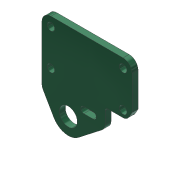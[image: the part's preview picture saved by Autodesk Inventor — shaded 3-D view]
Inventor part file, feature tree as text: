
AUTODESK INVENTOR PART (.ipt)
format: ipt  version: 2019.4 (Build 234330000, 330)  size: 136,192 bytes
history: native  units: mm
features: reference x8, other x7, sketch x1, extrude x1, hole x1
ambient origin geometry x8: Origin, YZ Plane, XZ Plane, XY Plane, X Axis, Y Axis, Z Axis, Center Point
bodies: Body1 (feature_tree)
feature tree (18):
  other  "ソリッド1"
  sketch  "スケッチ1"
  extrude  "押し出し1"  TaperAngle=30.0deg  [1 undecoded]
  hole  "穴1"  [1 undecoded]
  reference  "参照1"
  reference  "参照2"
  reference  "参照3"
  reference  "参照4"
  reference  "参照5"
  reference  "参照6"
  reference  "参照7"
  reference  "参照8"
  parser-record x1  (decoder bookkeeping rows leaked as tree rows — omitted from the tree; the rows remain in map.json)
  other  "COXA_UNIT_ASM.iam"
  other  "COXA_YAW_BLOCK_ASM2:1"
  other  "XM430_ASM_WITHOUT-BACK:1"
  other  "XM430_HOUSING_MIDDLE:1"
  other  "COXA_YAW_SERVO_BASE:1"
note: 2 required parameter values undecoded (feature->parameter linkage not recoverable at this tier; creation-order binding heuristic only, values carry confidence <= 0.55)
note: 1 file-system path scrubbed to <path> (originals preserved in map.json)
